FCSTD DOCUMENT  (FreeCAD 0.18R13588 (Git))
Label: footprint-template
License: All rights reserved
LicenseURL: http://en.wikipedia.org/wiki/All_rights_reserved
objects: Sketcher::SketchObject×5, App::Annotation×2, App::DocumentObjectGroup×1
note: 5 computed .brp shape members not serialized (recipe doc carries the construction recipe); baked Part::Feature solids carry a one-line shape summary decoded from their .brp

FEATURE [Sketcher::SketchObject] Sketch002  label="F_CrtYd_0.05"
  sketch-geometry (4):
    g0: LineSegment StartX=-31.8687 StartY=25.0862 StartZ=0 EndX=35.9152 EndY=25.0862 EndZ=0
    g1: LineSegment StartX=35.9152 StartY=25.0862 StartZ=0 EndX=35.9152 EndY=-14.4689 EndZ=0
    g2: LineSegment StartX=35.9152 StartY=-14.4689 StartZ=0 EndX=-31.8687 EndY=-14.4689 EndZ=0
    g3: LineSegment StartX=-31.8687 StartY=-14.4689 StartZ=0 EndX=-31.8687 EndY=25.0862 EndZ=0
  constraints (8):
    c: Coincident(g0,g1)
    c: Coincident(g1,g2)
    c: Coincident(g2,g3)
    c: Coincident(g3,g0)
    c: Horizontal(g0)
    c: Horizontal(g2)
    c: Vertical(g1)
    c: Vertical(g3)
FEATURE [Sketcher::SketchObject] Sketch003  label="F_Silks_0.16"
  sketch-geometry (9):
    g0: LineSegment StartX=-28 StartY=15 StartZ=0 EndX=-23 EndY=21 EndZ=0
    g1: LineSegment StartX=-23 StartY=21 StartZ=0 EndX=24 EndY=21 EndZ=0
    g2: LineSegment StartX=24 StartY=21 StartZ=0 EndX=32 EndY=11 EndZ=0
    g3: LineSegment StartX=32 StartY=11 StartZ=0 EndX=32 EndY=-11 EndZ=0
    g4: LineSegment StartX=32 StartY=-11 StartZ=0 EndX=-28 EndY=-11 EndZ=0
    g5: LineSegment StartX=-28 StartY=-11 StartZ=0 EndX=-28 EndY=15 EndZ=0
    g6: LineSegment StartX=0 StartY=-11 StartZ=0 EndX=32 EndY=11 EndZ=0
    g7: LineSegment StartX=17 StartY=-7 StartZ=0 EndX=26.1262 EndY=0.15587 EndZ=0
    g8: ArcOfCircle CenterX=21.5631 CenterY=-3.42207 CenterZ=0 NormalX=0 NormalY=0 NormalZ=1 AngleXU=0 Radius=5.79857 StartAngle=3.80656 EndAngle=6.94816
  constraints (15):
    c: Coincident(g0,g1)
    c: Horizontal(g1)
    c: Coincident(g1,g2)
    c: Coincident(g2,g3)
    c: Vertical(g3)
    c: Coincident(g3,g4)
    c: Horizontal(g4)
    c: Coincident(g4,g5)
    c: Coincident(g5,g0)
    c: Vertical(g5)
    c: Coincident(g6,g2)
    c: PointOnObject(g8,g7)
    c: Coincident(g8,g7)
    c: PointOnObject(g8,g7)
    c: Coincident(g7,g8)
FEATURE [Sketcher::SketchObject] Sketch004  label="F_Fab_0.1"
  sketch-geometry (6):
    g0: LineSegment StartX=-29 StartY=15 StartZ=0 EndX=-23 EndY=22.2167 EndZ=0
    g1: LineSegment StartX=-23 StartY=22.2167 StartZ=0 EndX=24 EndY=22.2167 EndZ=0
    g2: LineSegment StartX=24 StartY=22.2167 StartZ=0 EndX=33 EndY=11 EndZ=0
    g3: LineSegment StartX=33 StartY=11 StartZ=0 EndX=33 EndY=-12 EndZ=0
    g4: LineSegment StartX=33 StartY=-12 StartZ=0 EndX=-29 EndY=-12 EndZ=0
    g5: LineSegment StartX=-29 StartY=-12 StartZ=0 EndX=-29 EndY=15 EndZ=0
  constraints (10):
    c: Coincident(g0,g1)
    c: Horizontal(g1)
    c: Coincident(g1,g2)
    c: Coincident(g2,g3)
    c: Vertical(g3)
    c: Coincident(g3,g4)
    c: Horizontal(g4)
    c: Coincident(g4,g5)
    c: Coincident(g5,g0)
    c: Vertical(g5)
FEATURE [App::Annotation] Text  label="Ref#_1.0mm"
  LabelText = REF**
  Position = (0,17,0)
FEATURE [App::Annotation] Text001  label="Value#_0.8mm"
  LabelText = Value 
  Position = (11,-9,0)
FEATURE [Sketcher::SketchObject] Sketch011  label="Pads_TH_SMD"
  sketch-geometry (41):
    g0: Circle CenterX=0 CenterY=0 CenterZ=0 NormalX=0 NormalY=0 NormalZ=1 AngleXU=0 Radius=1.0754
    g1: Circle CenterX=3 CenterY=10.5347 CenterZ=0 NormalX=0 NormalY=0 NormalZ=1 AngleXU=0 Radius=1.02042
    g2: Circle CenterX=-21 CenterY=10 CenterZ=0 NormalX=0 NormalY=0 NormalZ=1 AngleXU=0 Radius=1.25054
    g3: ArcOfCircle CenterX=-20 CenterY=-5.55691 CenterZ=0 NormalX=0 NormalY=0 NormalZ=1 AngleXU=0 Radius=1.44309 StartAngle=1.5708 EndAngle=4.71239
    g4: ArcOfCircle CenterX=-17 CenterY=-5.55691 CenterZ=0 NormalX=0 NormalY=0 NormalZ=1 AngleXU=0 Radius=1.44309 StartAngle=4.71239 EndAngle=7.85398
    g5: LineSegment StartX=-20 StartY=-7 StartZ=0 EndX=-17 EndY=-7 EndZ=0
    g6: LineSegment StartX=-20 StartY=-4.11382 StartZ=0 EndX=-17 EndY=-4.11382 EndZ=0
    g7: ArcOfCircle CenterX=12 CenterY=10 CenterZ=0 NormalX=0 NormalY=0 NormalZ=1 AngleXU=0 Radius=1 StartAngle=1.5708 EndAngle=4.71239
    g8: ArcOfCircle CenterX=14 CenterY=10 CenterZ=0 NormalX=0 NormalY=0 NormalZ=1 AngleXU=0 Radius=1 StartAngle=4.71239 EndAngle=7.85398
    g9: LineSegment StartX=12 StartY=9 StartZ=0 EndX=14 EndY=9 EndZ=0
    g10: LineSegment StartX=12 StartY=11 StartZ=0 EndX=14 EndY=11 EndZ=0
    g11: LineSegment StartX=-3 StartY=2 StartZ=0 EndX=3 EndY=2 EndZ=0
    g12: LineSegment StartX=3 StartY=2 StartZ=0 EndX=3 EndY=-2 EndZ=0
    g13: LineSegment StartX=3 StartY=-2 StartZ=0 EndX=-3 EndY=-2 EndZ=0
    g14: LineSegment StartX=-3 StartY=-2 StartZ=0 EndX=-3 EndY=2 EndZ=0
    g15: LineSegment StartX=0 StartY=12 StartZ=0 EndX=5 EndY=12 EndZ=0
    g16: LineSegment StartX=5 StartY=12 StartZ=0 EndX=5 EndY=9 EndZ=0
    g17: LineSegment StartX=5 StartY=9 StartZ=0 EndX=0 EndY=9 EndZ=0
    g18: LineSegment StartX=0 StartY=9 StartZ=0 EndX=0 EndY=12 EndZ=0
    g19: LineSegment StartX=-23 StartY=-8 StartZ=0 EndX=-11 EndY=-8 EndZ=0
    g20: LineSegment StartX=-11 StartY=-8 StartZ=0 EndX=-11 EndY=0 EndZ=0
    g21: LineSegment StartX=-11 StartY=0 StartZ=0 EndX=-23 EndY=0 EndZ=0
    g22: LineSegment StartX=-23 StartY=0 StartZ=0 EndX=-23 EndY=-8 EndZ=0
    g23: Circle CenterX=-21 CenterY=10 CenterZ=0 NormalX=0 NormalY=0 NormalZ=1 AngleXU=0 Radius=2.23607
    g24: ArcOfCircle CenterX=12 CenterY=15 CenterZ=0 NormalX=0 NormalY=0 NormalZ=1 AngleXU=0 Radius=4 StartAngle=0 EndAngle=3.14159
    g25: ArcOfCircle CenterX=12 CenterY=10.3751 CenterZ=0 NormalX=0 NormalY=0 NormalZ=1 AngleXU=0 Radius=4 StartAngle=3.14159 EndAngle=6.28319
    g26: LineSegment StartX=8 StartY=15 StartZ=0 EndX=8 EndY=10.3751 EndZ=0
    g27: LineSegment StartX=16 StartY=15 StartZ=0 EndX=16 EndY=10.3751 EndZ=0
    g28: LineSegment StartX=-16 StartY=6 StartZ=0 EndX=-12 EndY=6 EndZ=0
    g29: LineSegment StartX=-12 StartY=6 StartZ=0 EndX=-12 EndY=3 EndZ=0
    g30: LineSegment StartX=-12 StartY=3 StartZ=0 EndX=-16 EndY=3 EndZ=0
    g31: LineSegment StartX=-16 StartY=3 StartZ=0 EndX=-16 EndY=6 EndZ=0
    g32: Circle CenterX=-14 CenterY=10 CenterZ=0 NormalX=0 NormalY=0 NormalZ=1 AngleXU=0 Radius=2
    g33: LineSegment StartX=6 StartY=3 StartZ=0 EndX=10 EndY=3 EndZ=0
    g34: LineSegment StartX=10 StartY=3 StartZ=0 EndX=10 EndY=-3 EndZ=0
    g35: LineSegment StartX=10 StartY=-3 StartZ=0 EndX=6 EndY=-3 EndZ=0
    g36: LineSegment StartX=6 StartY=-3 StartZ=0 EndX=6 EndY=3 EndZ=0
    g37: ArcOfCircle CenterX=19.3586 CenterY=9 CenterZ=0 NormalX=0 NormalY=0 NormalZ=1 AngleXU=0 Radius=2 StartAngle=1.5708 EndAngle=4.71239
    g38: ArcOfCircle CenterX=23.3586 CenterY=9 CenterZ=0 NormalX=0 NormalY=0 NormalZ=1 AngleXU=0 Radius=2 StartAngle=4.71239 EndAngle=7.85398
    g39: LineSegment StartX=19.3586 StartY=7 StartZ=0 EndX=23.3586 EndY=7 EndZ=0
    g40: LineSegment StartX=19.3586 StartY=11 StartZ=0 EndX=23.3586 EndY=11 EndZ=0
  constraints (57):
    c: Coincident(g0,g-1)
    c: Tangent(g3,g6) = 1.5708
    c: Tangent(g3,g5) = -1.5708
    c: Tangent(g5,g4) = -1.5708
    c: Tangent(g6,g4) = 1.5708
    c: Horizontal(g5)
    c: Equal(g3,g4)
    c: Tangent(g7,g10) = 1.5708
    c: Tangent(g7,g9) = -1.5708
    c: Tangent(g9,g8) = -1.5708
    c: Tangent(g10,g8) = 1.5708
    c: Horizontal(g9)
    c: Equal(g7,g8)
    c: Coincident(g11,g12)
    c: Coincident(g12,g13)
    c: Coincident(g13,g14)
    c: Coincident(g14,g11)
    c: Horizontal(g11)
    c: Horizontal(g13)
    c: Vertical(g12)
    c: Vertical(g14)
    c: Coincident(g19,g20)
    c: Coincident(g20,g21)
    c: Coincident(g21,g22)
    c: Coincident(g22,g19)
    c: Horizontal(g19)
    c: Horizontal(g21)
    c: Vertical(g20)
    c: Vertical(g22)
    c: Tangent(g24,g27) = 1.5708
    c: Tangent(g24,g26) = -1.5708
    c: Tangent(g26,g25) = -1.5708
    c: Tangent(g27,g25) = 1.5708
    c: Vertical(g26)
    c: Equal(g24,g25)
    c: Coincident(g28,g29)
    c: Coincident(g29,g30)
    c: Coincident(g30,g31)
    c: Coincident(g31,g28)
    c: Horizontal(g28)
    c: Horizontal(g30)
    c: Vertical(g29)
    c: Vertical(g31)
    c: Coincident(g33,g34)
    c: Coincident(g34,g35)
    c: Coincident(g35,g36)
    c: Coincident(g36,g33)
    c: Horizontal(g33)
    c: Horizontal(g35)
    c: Vertical(g34)
    c: Vertical(g36)
    c: Tangent(g37,g40) = 1.5708
    c: Tangent(g37,g39) = -1.5708
    c: Tangent(g39,g38) = -1.5708
    c: Tangent(g40,g38) = 1.5708
    c: Horizontal(g39)
    c: Equal(g37,g38)
FEATURE [Sketcher::SketchObject] Sketch  label="Pads_NPTH"
  sketch-geometry (8):
    g0: Circle CenterX=23.5 CenterY=-5.5 CenterZ=0 NormalX=0 NormalY=0 NormalZ=1 AngleXU=0 Radius=2.23607
    g1: Circle CenterX=-10 CenterY=17 CenterZ=0 NormalX=0 NormalY=0 NormalZ=1 AngleXU=0 Radius=1.8
    g2: Circle CenterX=23.5 CenterY=-5.5 CenterZ=0 NormalX=0 NormalY=0 NormalZ=1 AngleXU=0 Radius=1
    g3: ArcOfCircle CenterX=-5.9383 CenterY=-6.4555 CenterZ=0 NormalX=0 NormalY=0 NormalZ=1 AngleXU=0 Radius=2.81425 StartAngle=1.5708 EndAngle=4.71239
    g4: ArcOfCircle CenterX=-2.04596 CenterY=-6.4555 CenterZ=0 NormalX=0 NormalY=0 NormalZ=1 AngleXU=0 Radius=2.81425 StartAngle=4.71239 EndAngle=7.85398
    g5: LineSegment StartX=-5.9383 StartY=-9.26976 StartZ=0 EndX=-2.04596 EndY=-9.26976 EndZ=0
    g6: LineSegment StartX=-5.9383 StartY=-3.64125 StartZ=0 EndX=-2.04596 EndY=-3.64125 EndZ=0
    g7: Circle CenterX=-5.9383 CenterY=-6.39562 CenterZ=0 NormalX=0 NormalY=0 NormalZ=1 AngleXU=0 Radius=1.3295
  constraints (7):
    c: Radius(g1) = 1.8
    c: Tangent(g3,g6) = 1.5708
    c: Tangent(g3,g5) = -1.5708
    c: Tangent(g5,g4) = -1.5708
    c: Tangent(g6,g4) = 1.5708
    c: Horizontal(g5)
    c: Equal(g3,g4)
FEATURE [App::DocumentObjectGroup] Group  label="footprint_template"
  Group = -> [Sketch002,Sketch003,Sketch004,Sketch011,Sketch,Text,Text001]
